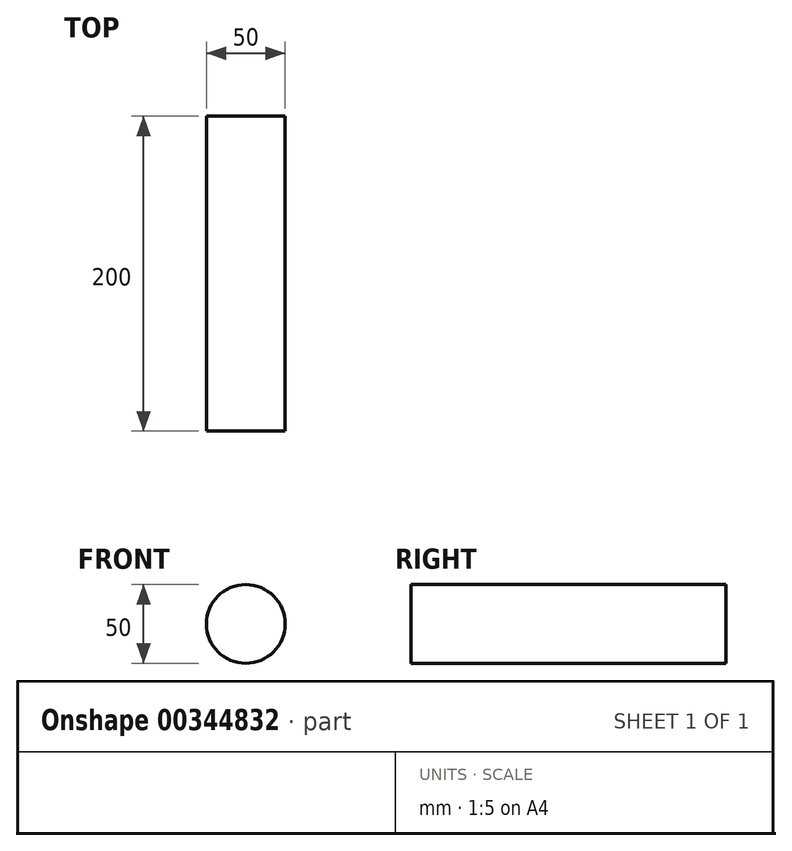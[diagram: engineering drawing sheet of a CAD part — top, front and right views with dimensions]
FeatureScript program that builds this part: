
annotation { "Feature Type Name" : "Feature", "Feature Type Description" : "" }
export const myFeature = defineFeature(function(context is Context, id is Id, definition is map)
    precondition{}
    {
        {
            var Q0;
            Q0=qCreatedBy(makeId("Front.planeOp"),FACE);
            var sketch = newSketch(context, id + "F0", { "sketchPlane" : qUnion([Q0])});
            skCircle(sketch, "E0", {"center": v(0, 0) * mm, "radius": 25 * mm});
            skSolve(sketch);
        }
        {
            var Q0;
            Q0=makeQuery(id+"F0.imprint","IMPRINT",FACE,{"disambiguationData":[TD([[makeQuery(id+"F0.imprint","IMPRINT",EDGE,{"derivedFrom":sQuery(id+"F0.wireOp",EDGE,"E0")}),1.0]])]});
            extrude(context, id + "F1", {"entities" : qUnion([Q0]), "endBound" : BoundingType.SYMMETRIC, "depth" : 200 * mm});
        }
    });
